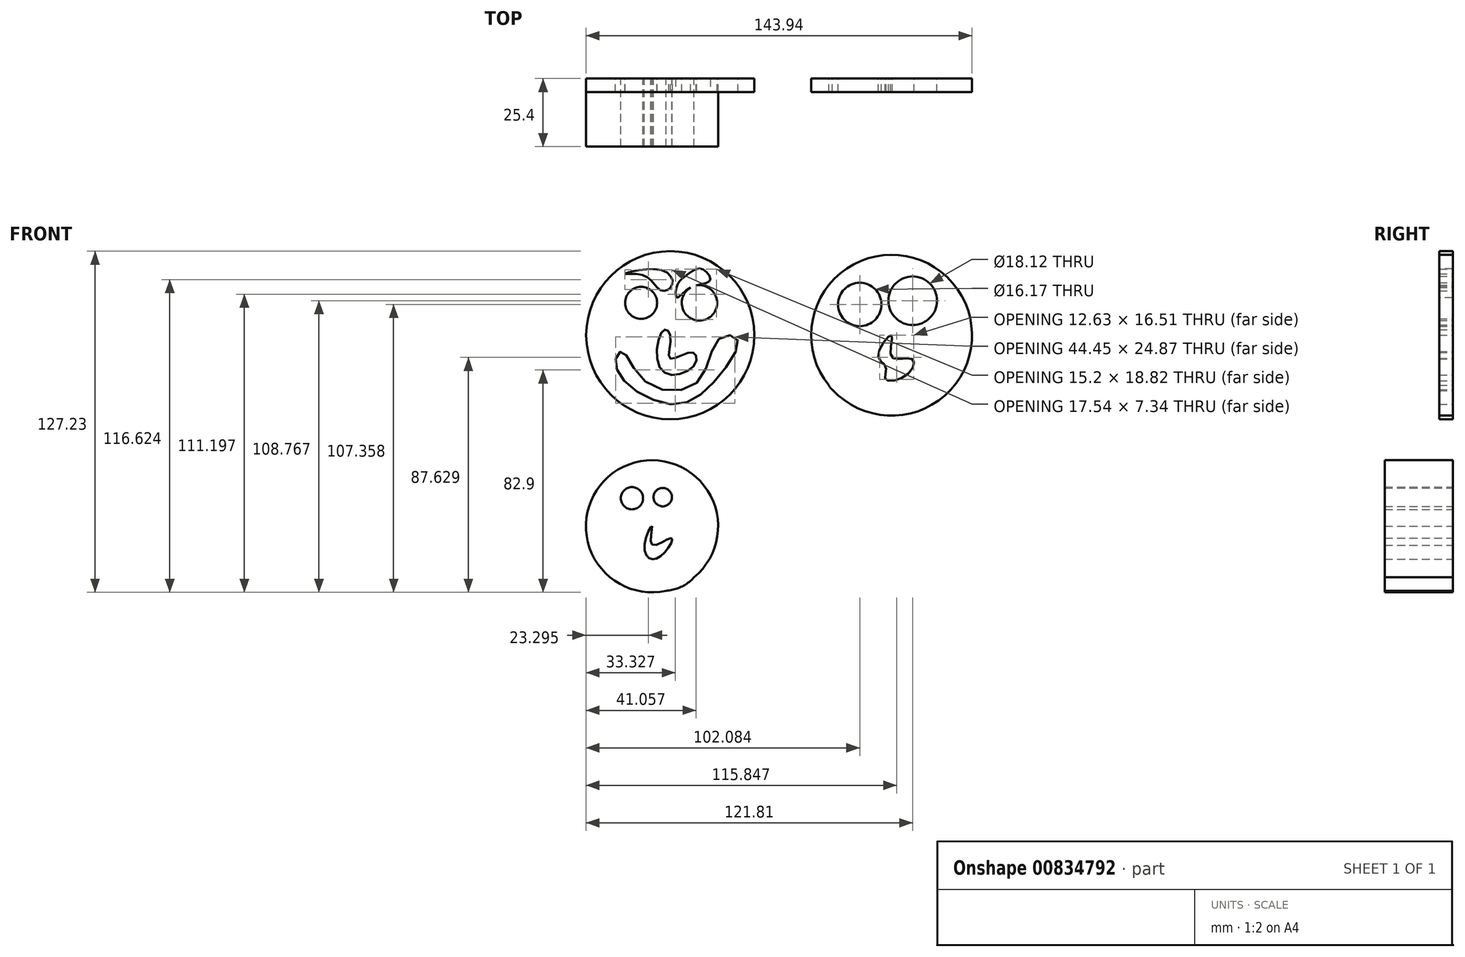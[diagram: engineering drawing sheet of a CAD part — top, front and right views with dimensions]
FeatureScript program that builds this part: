
annotation { "Feature Type Name" : "Feature", "Feature Type Description" : "" }
export const myFeature = defineFeature(function(context is Context, id is Id, definition is map)
    precondition{}
    {
        {
            var Q0;
            Q0=qCreatedBy(makeId("Front.planeOp"),FACE);
            var sketch = newSketch(context, id + "F0", { "sketchPlane" : qUnion([Q0])});
            skCircle(sketch, "E0", {"center": v(-43.38, 43.07) * mm, "radius": 31.34 * mm});
            skCircle(sketch, "E1", {"center": v(-54.25, 55.15) * mm, "radius": 5.96 * mm});
            skCircle(sketch, "E2", {"center": v(-32.5, 55.15) * mm, "radius": 6.6 * mm});
            skFitSpline(sketch, "E3", {"points": [v(-43.38, 43.07) * mm, v(-43.38, 34.42) * mm, v(-35.12, 36.63) * mm, v(-34.32, 32) * mm, v(-46.4, 29.79) * mm, v(-46, 44.89) * mm, v(-43.38, 43.07) * mm]});
            skFitSpline(sketch, "E4", {"points": [v(-63.7, 34.22) * mm, v(-59.88, 25.36) * mm, v(-40.96, 17.31) * mm, v(-25.46, 27.58) * mm, v(-18.42, 41.67) * mm, v(-25.06, 41.87) * mm, v(-33.31, 25.56) * mm, v(-52.84, 25.97) * mm, v(-61.3, 37.04) * mm, v(-63.7, 34.22) * mm]});
            skFitSpline(sketch, "E5", {"points": [v(-60.28, 66.02) * mm, v(-46.2, 67.23) * mm, v(-42.77, 61.6) * mm, v(-46.8, 59.78) * mm, v(-52.84, 65.22) * mm, v(-60.28, 66.02) * mm]});
            skFitSpline(sketch, "E6", {"points": [v(-31.7, 67.83) * mm, v(-37.34, 65.42) * mm, v(-40.76, 61.8) * mm, v(-40.96, 57.16) * mm, v(-35.86, 60.83) * mm, v(-28.48, 63.6) * mm, v(-31.7, 67.83) * mm]});
            skSolve(sketch);
        }
        {
            var Q0;
            Q0 = qSketchRegion(id + "F0", true);
            extrude(context, id + "F1", {"entities" : qUnion([Q0]), "depth" : 5.08 * mm, "offsetDistance" : 25.4 * mm});
        }
        {
            var Q0;
            Q0=qCreatedBy(makeId("Front.planeOp"),FACE);
            var sketch = newSketch(context, id + "F2", { "sketchPlane" : qUnion([Q0])});
            skCircle(sketch, "E7", {"center": v(39.15, 43.07) * mm, "radius": 29.98 * mm});
            skCircle(sketch, "E8", {"center": v(27.27, 54.55) * mm, "radius": 8.08 * mm});
            skCircle(sketch, "E9", {"center": v(47, 55.96) * mm, "radius": 9.06 * mm});
            skFitSpline(sketch, "E10", {"points": [v(39.15, 43.07) * mm, v(34.12, 35.63) * mm, v(36.94, 31.2) * mm, v(36.94, 26.57) * mm, v(45.39, 28.78) * mm, v(46.8, 34.22) * mm, v(39.15, 35.02) * mm, v(39.15, 43.07) * mm]});
            skFitSpline(sketch, "E11", {"points": [v(19.22, 35.02) * mm, v(29.49, 30.2) * mm, v(39.15, 22.74) * mm, v(51.83, 27.58) * mm, v(55.65, 32.8) * mm, v(60.28, 36.63) * mm, v(62.7, 28.78) * mm, v(49.21, 19.52) * mm, v(42.77, 19.52) * mm, v(31.9, 18.52) * mm, v(26.67, 19.73) * mm, v(15.7, 24.38) * mm, v(19.22, 35.02) * mm]});
            skSolve(sketch);
        }
        {
            var Q0;
            Q0 = qSketchRegion(id + "F2", true);
            extrude(context, id + "F3", {"entities" : qUnion([Q0]), "depth" : 5.08 * mm, "offsetDistance" : 25.4 * mm});
        }
        {
            var Q0;
            Q0=qCreatedBy(makeId("Front.planeOp"),FACE);
            var sketch = newSketch(context, id + "F4", { "sketchPlane" : qUnion([Q0])});
            skCircle(sketch, "E12", {"center": v(-50.18, -28.18) * mm, "radius": 24.63 * mm});
            skCircle(sketch, "E13", {"center": v(-57.67, -17.71) * mm, "radius": 4.15 * mm});
            skCircle(sketch, "E14", {"center": v(-46.2, -17.31) * mm, "radius": 3.43 * mm});
            skFitSpline(sketch, "E15", {"points": [v(-50.18, -28.18) * mm, v(-53.04, -35.43) * mm, v(-50.18, -40.46) * mm, v(-44.38, -36.63) * mm, v(-42.97, -32.6) * mm, v(-50.18, -35.02) * mm, v(-50.18, -28.18) * mm]});
            skFitSpline(sketch, "E16", {"points": [v(-68.54, -36.63) * mm, v(-56.66, -43.88) * mm, v(-40.56, -42.67) * mm, v(-31.1, -33.82) * mm, v(-34.53, -47.2) * mm, v(-58.07, -49.11) * mm, v(-68.54, -36.63) * mm]});
            skSolve(sketch);
        }
        {
            var Q0;
            Q0 = qSketchRegion(id + "F4", true);
            extrude(context, id + "F5", {"entities" : qUnion([Q0]), "depth" : 25.4 * mm, "offsetDistance" : 25.4 * mm});
        }
    });
